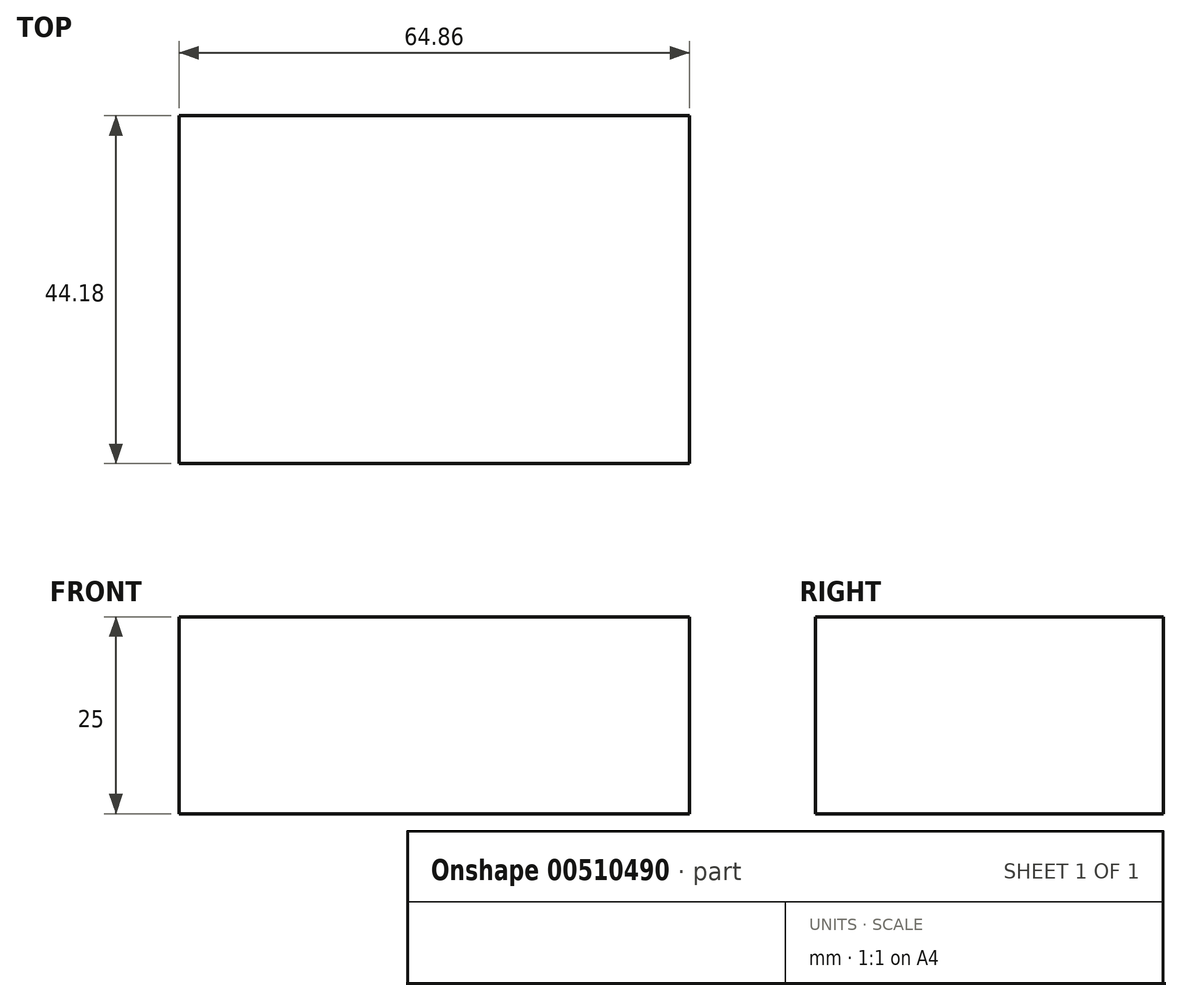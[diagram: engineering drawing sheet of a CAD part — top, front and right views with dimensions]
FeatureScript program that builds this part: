
annotation { "Feature Type Name" : "Feature", "Feature Type Description" : "" }
export const myFeature = defineFeature(function(context is Context, id is Id, definition is map)
    precondition{}
    {
        {
            var Q0;
            Q0=qCreatedBy(makeId("Top.planeOp"),FACE);
            var sketch = newSketch(context, id + "F0", { "sketchPlane" : qUnion([Q0])});
            skLineSegment(sketch, "E0.bottom", {"start": v(-32.43, 22.1) * mm, "end": v(32.43, 22.1) * mm});
            skLineSegment(sketch, "E0.top", {"start": v(-32.43, -22.1) * mm, "end": v(32.43, -22.1) * mm});
            skLineSegment(sketch, "E0.left", {"start": v(-32.43, 22.1) * mm, "end": v(-32.43, -22.1) * mm});
            skLineSegment(sketch, "E0.right", {"start": v(32.43, 22.1) * mm, "end": v(32.43, -22.1) * mm});
            skPoint(sketch, "E0.middle", {"position": v(0, 0) * mm});
            skSolve(sketch);
        }
        {
            var Q0;
            Q0 = qSketchRegion(id + "F0", true);
            extrude(context, id + "F1", {"entities" : qUnion([Q0]), "depth" : 25 * mm});
        }
    });
